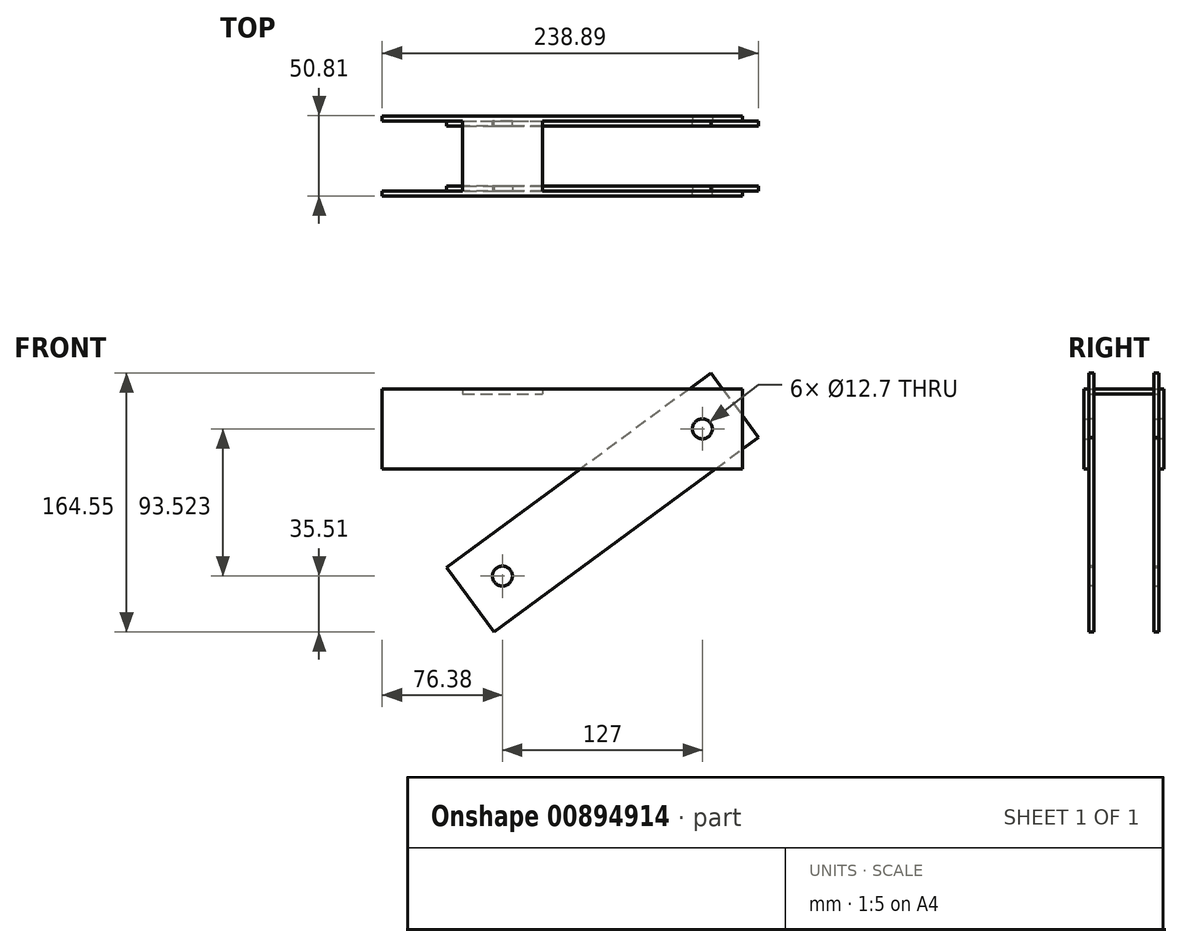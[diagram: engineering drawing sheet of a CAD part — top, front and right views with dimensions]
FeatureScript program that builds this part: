
annotation { "Feature Type Name" : "Feature", "Feature Type Description" : "" }
export const myFeature = defineFeature(function(context is Context, id is Id, definition is map)
    precondition{}
    {
        {
            var Q0;
            Q0=qCreatedBy(makeId("Front.planeOp"),FACE);
            var sketch = newSketch(context, id + "F0", { "sketchPlane" : qUnion([Q0])});
            skCircle(sketch, "E0", {"center": v(0, 0) * mm, "radius": 6.35 * mm});
            skLineSegment(sketch, "E1", {"start": v(132.4, 129.04) * mm, "end": v(-35.51, 5.4) * mm});
            skLineSegment(sketch, "E2", {"start": v(-35.51, 5.4) * mm, "end": v(-5.4, -35.51) * mm});
            skLineSegment(sketch, "E3", {"start": v(-5.4, -35.51) * mm, "end": v(162.51, 88.13) * mm});
            skLineSegment(sketch, "E4", {"start": v(132.4, 129.04) * mm, "end": v(162.51, 88.13) * mm});
            skCircle(sketch, "E5", {"center": v(127, 93.52) * mm, "radius": 6.35 * mm});
            skLineSegment(sketch, "E6.bottom", {"start": v(-76.38, 118.92) * mm, "end": v(152.4, 118.92) * mm});
            skLineSegment(sketch, "E6.top", {"start": v(-76.38, 68.12) * mm, "end": v(152.4, 68.12) * mm});
            skLineSegment(sketch, "E6.left", {"start": v(-76.38, 118.92) * mm, "end": v(-76.38, 68.12) * mm});
            skLineSegment(sketch, "E6.right", {"start": v(152.4, 118.92) * mm, "end": v(152.4, 68.12) * mm});
            skPoint(sketch, "E7", {"position": v(152.4, 93.52) * mm});
            skLineSegment(sketch, "E8", {"start": v(0, 0) * mm, "end": v(15.06, -20.45) * mm, "construction": true});
            skLineSegment(sketch, "E9.bottom", {"start": v(-25.4, 118.92) * mm, "end": v(25.4, 118.92) * mm});
            skLineSegment(sketch, "E9.top", {"start": v(-25.4, 115.75) * mm, "end": v(25.4, 115.75) * mm});
            skLineSegment(sketch, "E9.left", {"start": v(-25.4, 118.92) * mm, "end": v(-25.4, 115.75) * mm});
            skLineSegment(sketch, "E9.right", {"start": v(25.4, 118.92) * mm, "end": v(25.4, 115.75) * mm});
            skLineSegment(sketch, "E10", {"start": v(7.53, 37.1) * mm, "end": v(9.42, 34.53) * mm});
            skLineSegment(sketch, "E11", {"start": v(9.42, 34.53) * mm, "end": v(50.32, 64.66) * mm});
            skLineSegment(sketch, "E12", {"start": v(48.44, 67.21) * mm, "end": v(50.32, 64.66) * mm});
            skPoint(sketch, "E13", {"position": v(0, 115.75) * mm});
            skSolve(sketch);
        }
        {
            var Q0;
            {var subQ0=sQuery(id+"F0.wireOp",EDGE,"E1");var subQ1=sQuery(id+"F0.wireOp",EDGE,"ygqzxqpk-h8sy-JIl8-c7l7-SKNyjYcmnEdw");var subQ2=makeQuery(id+"F0.imprint","INTERSECT",VERTEX,{"derivedFrom":[subQ1,subQ0]});Q0=makeQuery(id+"F0.imprint","IMPRINT",FACE,{"disambiguationData":[TD([[makeQuery(id+"F0.imprint","IMPRINT",EDGE,{"disambiguationData":[TD([[subQ2,1.0]])],"derivedFrom":subQ1}),-1.0]])]});}
            var Q1;
            Q1=makeQuery(id+"F0.imprint","IMPRINT",FACE,{"disambiguationData":[TD([[makeQuery(id+"F0.imprint","IMPRINT",EDGE,{"derivedFrom":sQuery(id+"F0.wireOp",EDGE,"E5")}),-1.0]])]});
            var Q2;
            {var subQ0=sQuery(id+"F0.wireOp",EDGE,"E4");var subQ1=sQuery(id+"F0.wireOp",EDGE,"E3");var subQ2=makeQuery(id+"F0.imprint","INTERSECT",VERTEX,{"derivedFrom":[subQ1,subQ0]});Q2=makeQuery(id+"F0.imprint","IMPRINT",FACE,{"disambiguationData":[TD([[makeQuery(id+"F0.imprint","IMPRINT",EDGE,{"disambiguationData":[TD([[subQ2,1.0]])],"derivedFrom":subQ1}),1.0]])]});}
            var Q3;
            {var subQ0=sQuery(id+"F0.wireOp",EDGE,"E6.bottom");var subQ1=sQuery(id+"F0.wireOp",EDGE,"E1");var subQ2=makeQuery(id+"F0.imprint","INTERSECT",VERTEX,{"derivedFrom":[subQ1,subQ0]});Q3=makeQuery(id+"F0.imprint","IMPRINT",FACE,{"disambiguationData":[TD([[makeQuery(id+"F0.imprint","IMPRINT",EDGE,{"disambiguationData":[TD([[subQ2,1.0]])],"derivedFrom":subQ1}),1.0]])]});}
            var Q4;
            Q4=makeQuery(id+"F0.imprint","IMPRINT",FACE,{"disambiguationData":[TD([[makeQuery(id+"F0.imprint","IMPRINT",EDGE,{"derivedFrom":sQuery(id+"F0.wireOp",EDGE,"E0")}),-1.0]])]});
            var Q5;
            {var subQ2=sQuery(id+"F0.wireOp",EDGE,"E10");Q5=makeQuery(id+"F0.imprint","IMPRINT",FACE,{"disambiguationData":[TD([[makeQuery(id+"F0.imprint","IMPRINT",EDGE,{"derivedFrom":subQ2}),1.0]])]});}
            extrude(context, id + "F1", {"entities" : qUnion([Q0, Q1, Q2, Q3, Q4, Q5]), "depth" : 3.17 * mm, "offsetDistance" : 25.4 * mm});
        }
        {
            var Q0;
            {var subQ0=sQuery(id+"F0.wireOp",EDGE,"E6.left");Q0=makeQuery(id+"F0.imprint","IMPRINT",FACE,{"disambiguationData":[TD([[makeQuery(id+"F0.imprint","IMPRINT",EDGE,{"derivedFrom":subQ0}),1.0]])]});}
            var Q1;
            Q1=makeQuery(id+"F0.imprint","IMPRINT",FACE,{"disambiguationData":[TD([[makeQuery(id+"F0.imprint","IMPRINT",EDGE,{"derivedFrom":sQuery(id+"F0.wireOp",EDGE,"E5")}),-1.0]])]});
            var Q2;
            {var subQ0=sQuery(id+"F0.wireOp",EDGE,"E6.top");var subQ1=sQuery(id+"F0.wireOp",EDGE,"E3");var subQ2=makeQuery(id+"F0.imprint","INTERSECT",VERTEX,{"derivedFrom":[subQ1,subQ0]});Q2=makeQuery(id+"F0.imprint","IMPRINT",FACE,{"disambiguationData":[TD([[makeQuery(id+"F0.imprint","IMPRINT",EDGE,{"disambiguationData":[TD([[subQ2,-1.0]])],"derivedFrom":subQ1}),-1.0]])]});}
            var Q3;
            {var subQ0=sQuery(id+"F0.wireOp",EDGE,"E6.bottom");var subQ1=sQuery(id+"F0.wireOp",EDGE,"E4");var subQ2=makeQuery(id+"F0.imprint","INTERSECT",VERTEX,{"derivedFrom":[subQ1,subQ0]});Q3=makeQuery(id+"F0.imprint","IMPRINT",FACE,{"disambiguationData":[TD([[makeQuery(id+"F0.imprint","IMPRINT",EDGE,{"disambiguationData":[TD([[subQ2,-1.0]])],"derivedFrom":subQ1}),1.0]])]});}
            var Q4;
            Q4=makeQuery(id+"F0.imprint","IMPRINT",FACE,{"disambiguationData":[TD([[makeQuery(id+"F0.imprint","IMPRINT",EDGE,{"derivedFrom":sQuery(id+"F0.wireOp",EDGE,"E9.top")}),1.0]])]});
            extrude(context, id + "F2", {"entities" : qUnion([Q0, Q1, Q2, Q3, Q4]), "oppositeDirection" : true, "depth" : 3.17 * mm, "offsetDistance" : 25.4 * mm});
        }
        {
            var Q0;
            Q0=makeQuery(id+"F1.opExtrude","CAP_FACE",FACE,{"disambiguationData":[OSD([sQuery(id+"F0.wireOp",EDGE,"E0"),sQuery(id+"F0.wireOp",EDGE,"E1"),sQuery(id+"F0.wireOp",EDGE,"E2"),sQuery(id+"F0.wireOp",EDGE,"E3"),sQuery(id+"F0.wireOp",EDGE,"E4"),sQuery(id+"F0.wireOp",EDGE,"E5")])],"isStart":false});
            cPlane(context, id + "F3", {"entities" : qUnion([Q0]), "cplaneType" : CPlaneType.OFFSET, "offset" : 19.05 * mm, "width" : 152.4 * mm, "height" : 152.4 * mm});
        }
        {
            var Q0;
            Q0=makeQuery(id+"F1.opExtrude","SWEPT_BODY",BODY,{"disambiguationData":[OSD([sQuery(id+"F0.wireOp",EDGE,"E0"),sQuery(id+"F0.wireOp",EDGE,"E1"),sQuery(id+"F0.wireOp",EDGE,"E2"),sQuery(id+"F0.wireOp",EDGE,"E3"),sQuery(id+"F0.wireOp",EDGE,"E4"),sQuery(id+"F0.wireOp",EDGE,"E5")])]});
            var Q1;
            Q1=makeQuery(id+"F2.opExtrude","SWEPT_BODY",BODY,{"disambiguationData":[OSD([sQuery(id+"F0.wireOp",EDGE,"E5"),sQuery(id+"F0.wireOp",EDGE,"E6.bottom"),sQuery(id+"F0.wireOp",EDGE,"E6.top"),sQuery(id+"F0.wireOp",EDGE,"E6.left"),sQuery(id+"F0.wireOp",EDGE,"E6.right")])]});
            var Q2;
            Q2=qCreatedBy(id+"F3.planeOp",FACE);
            mirror(context, id + "F4", {"entities" : qUnion([Q0, Q1]), "mirrorPlane" : qUnion([Q2])});
        }
        {
            var Q0;
            Q0=makeQuery(id+"F0.imprint","IMPRINT",FACE,{"disambiguationData":[TD([[makeQuery(id+"F0.imprint","IMPRINT",EDGE,{"derivedFrom":sQuery(id+"F0.wireOp",EDGE,"E9.top")}),1.0]])]});
            var Q1;
            Q1=makeQuery(id+"F4.opPattern","COPY",FACE,{"derivedFrom":makeQuery(id+"F2.opExtrude","CAP_FACE",FACE,{"disambiguationData":[OSD([sQuery(id+"F0.wireOp",EDGE,"E5"),sQuery(id+"F0.wireOp",EDGE,"E6.bottom"),sQuery(id+"F0.wireOp",EDGE,"E6.top"),sQuery(id+"F0.wireOp",EDGE,"E6.left"),sQuery(id+"F0.wireOp",EDGE,"E6.right")])],"isStart":true}),"instanceName":"1"});
            extrude(context, id + "F5", {"entities" : qUnion([Q0]), "operationType" : NewBodyOperationType.ADD, "endBound" : BoundingType.UP_TO_SURFACE, "depth" : 25.4 * mm, "endBoundEntityFace" : qUnion([Q1]), "offsetDistance" : 25.4 * mm});
        }
    });
